# Revit family: BE_22365_de_DE
name_source: partatom
category: Leuchten
revit_build: Autodesk Revit 2015 (Build: 20150704_0715(x64)
units: mm (PartAtom-declared; Revit-internal decimal feet)

## types (6) — shared parameters
AC/DC = AC/DC
Aktualisierung = 2016-06-09T04:10:41
BEGA_Dummy = Nein
BEGA_IES = Ja
BEGA_Intern = Ja
BEGA_Intern_Konstruktion = Ja
BEGA_Intern_an = Ja
BEGA_Intern_aus = Ja
Befestigungsabstand = 274 mm
Befestigungsbohrung = Ø 5 mm
Beschreibung = Wandleuchte
Beschreibung_Sonderanfertigung = Hier können Sie Informationen zur Sonderanfertigung eintragen.
CE_Konformität = ja
Energieeffizienzklasse = LED A++ - A
Farbfilter = 16777215
Farbtemperaturverschiebung bei Dämpfen der Lampe = <Keine Auswahl>
Farbwiedergabeindex = Ra > 80
Frequenz = 0/50-60 Hz
Gewicht = 1.95 kg
Hersteller = BEGA
Lampe = LED 21 W
Lastklassifizierung = Beleuchtung
Lebensdauerkriterien = L70 = 50.000 h
Logo = BEGA_Logo.png
Material_02 = BEGA_Oberfläche_Silber_matt
Material_03 = BEGA_Oberfläche_Weiss_matt
Material_06 = BEGA_Oberfläche_Edelstahl_gebürstet
Material_10 = BEGA_Glas_matt
Neigungswinkel = 0.00°
Produktdatenblatt = http://www.bega.de
Scheinlast = 0 VA
Schutzart = IP 65
Schutzklasse = I
Sonderanfertigung = Nein
Spannung = 0 V
Typenbild = 22365.png
URL = http://www.bega.de
zero-valued in all types: Vorgabe-Ansicht

## per-type parameters (varying)
| type | Bestellnummer | Datei für fotometrisches Netz | Farbtemperatur | LED_Modulbezeichnung | Lampenlichtstrom | Leuchtenlichtstrom | M_A | M_G | M_W | Modell |
| BEGA_22365_Silber_K3 | 22365A | BE_22365.IES | 3000 K | 2xLED-0269/830 | 2460 lm | 1334 lm | Ja | Nein | Nein | 22365A |
| BEGA_22365_Weiß_K3 | 22365W | BE_22365.IES | 3000 K | 2xLED-0269/830 | 2460 lm | 1334 lm | Nein | Nein | Ja | 22365W |
| BEGA_22365_Weiß_K4 | 22365WK4 | BE_22365K4.IES | 4000 K | 2xLED-0269/840 | 2640 lm | 1431 lm | Nein | Nein | Ja | 22365WK4 |
| BEGA_22365_Grafit_K4 | 22365K4 | BE_22365K4.IES | 4000 K | 2xLED-0269/840 | 2640 lm | 1431 lm | Nein | Ja | Nein | 22365K4 |
| BEGA_22365_Silber_K4 | 22365AK4 | BE_22365K4.IES | 4000 K | 2xLED-0269/840 | 2640 lm | 1431 lm | Ja | Nein | Nein | 22365AK4 |
| BEGA_22365_Grafit_K3 | 22365 | BE_22365.IES | 3000 K | 2xLED-0269/830 | 2460 lm | 1334 lm | Nein | Ja | Nein | 22365 |
